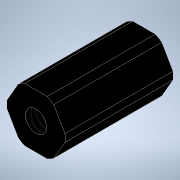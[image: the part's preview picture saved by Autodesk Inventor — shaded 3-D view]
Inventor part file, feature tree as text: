
AUTODESK INVENTOR PART (.ipt)
format: ipt  version: 2022.3 (Build 263350000, 350)  size: 113,664 bytes
history: native  units: in
note: dims shown in document units (in); Inventor stores cm internally (conversion verified against a paired STEP export)
features: sketch x2, extrude x1, hole x1
ambient origin geometry x8: Origin, YZ Plane, XZ Plane, XY Plane, X Axis, Y Axis, Z Axis, Center Point
bodies: Solid1 (feature_tree)
feature tree (4):
  extrude  "Extrusion1"  Depth=0.5in
  hole  "Hole1"  [1 undecoded]
  sketch  "Sketch1"  dims[d0=0.5in d1=0.5413in]
  sketch  "Sketch2"  dims[d2=1.0in d3=0.0in d4=0.196in d5=0.5in d6=0.507in d7=0.25in d8=0.5635in d9=1.0in d10=0.8108in]
note: 1 required parameter value undecoded (feature->parameter linkage not recoverable at this tier; creation-order binding heuristic only, values carry confidence <= 0.55)
